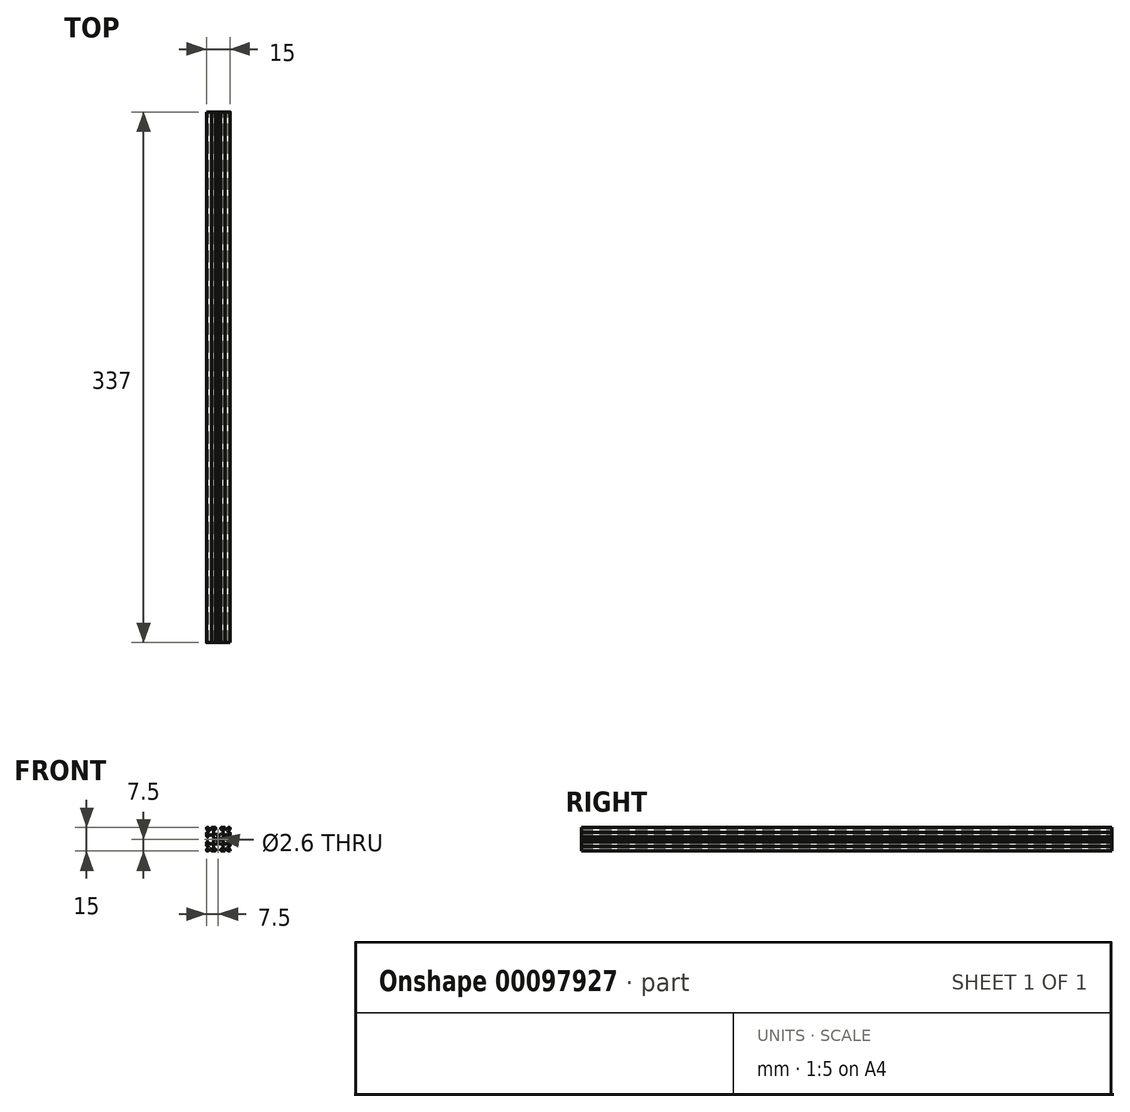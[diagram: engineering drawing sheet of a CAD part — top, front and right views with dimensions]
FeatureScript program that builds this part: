
annotation { "Feature Type Name" : "Feature", "Feature Type Description" : "" }
export const myFeature = defineFeature(function(context is Context, id is Id, definition is map)
    precondition{}
    {
        {
            var Q0;
            Q0=qCreatedBy(makeId("Front.planeOp"),FACE);
            var sketch = newSketch(context, id + "F0", { "sketchPlane" : qUnion([Q0])});
            skLineSegment(sketch, "E0.0.0", {"start": v(0.83, -2.55) * mm, "end": v(0.83, -2.77) * mm});
            skArc(sketch, "E0.0.1", {"start": v(0.83, -2.77) * mm, "mid": v(0.87, -2.9) * mm, "end": v(0.98, -2.97) * mm});
            skLineSegment(sketch, "E0.0.2", {"start": v(0.98, -2.97) * mm, "end": v(2.5, -3.31) * mm});
            skArc(sketch, "E0.0.3", {"start": v(2.5, -3.31) * mm, "mid": v(2.8, -3.49) * mm, "end": v(2.9, -3.8) * mm});
            skLineSegment(sketch, "E0.0.4", {"start": v(2.9, -3.8) * mm, "end": v(2.9, -5.9) * mm});
            skArc(sketch, "E0.0.5", {"start": v(2.9, -5.9) * mm, "mid": v(2.84, -6.04) * mm, "end": v(2.7, -6.1) * mm});
            skLineSegment(sketch, "E0.0.6", {"start": v(2.7, -6.1) * mm, "end": v(2.1, -6.1) * mm});
            skArc(sketch, "E0.0.7", {"start": v(2.1, -6.1) * mm, "mid": v(1.75, -6.25) * mm, "end": v(1.6, -6.6) * mm});
            skLineSegment(sketch, "E0.0.8", {"start": v(1.6, -6.6) * mm, "end": v(1.6, -7) * mm});
            skArc(sketch, "E0.0.9", {"start": v(1.6, -7) * mm, "mid": v(1.75, -7.35) * mm, "end": v(2.1, -7.5) * mm});
            skLineSegment(sketch, "E0.0.10", {"start": v(2.1, -7.5) * mm, "end": v(3.9, -7.5) * mm});
            skArc(sketch, "E0.0.11", {"start": v(3.9, -7.5) * mm, "mid": v(4.25, -7.35) * mm, "end": v(4.4, -7) * mm});
            skLineSegment(sketch, "E0.0.12", {"start": v(4.4, -7) * mm, "end": v(4.4, -6.67) * mm});
            skArc(sketch, "E0.0.13", {"start": v(4.4, -6.67) * mm, "mid": v(4.7, -6.2) * mm, "end": v(5.25, -6.31) * mm});
            skLineSegment(sketch, "E0.0.14", {"start": v(5.25, -6.31) * mm, "end": v(6.3, -7.35) * mm});
            skArc(sketch, "E0.0.15", {"start": v(6.3, -7.35) * mm, "mid": v(6.46, -7.46) * mm, "end": v(6.65, -7.5) * mm});
            skLineSegment(sketch, "E0.0.16", {"start": v(6.65, -7.5) * mm, "end": v(7.25, -7.5) * mm});
            skArc(sketch, "E0.0.17", {"start": v(7.25, -7.5) * mm, "mid": v(7.43, -7.43) * mm, "end": v(7.5, -7.25) * mm});
            skLineSegment(sketch, "E0.0.18", {"start": v(7.5, -7.25) * mm, "end": v(7.5, -6.65) * mm});
            skArc(sketch, "E0.0.19", {"start": v(7.5, -6.65) * mm, "mid": v(7.46, -6.46) * mm, "end": v(7.35, -6.3) * mm});
            skLineSegment(sketch, "E0.0.20", {"start": v(7.35, -6.3) * mm, "end": v(6.31, -5.25) * mm});
            skArc(sketch, "E0.0.21", {"start": v(6.31, -5.25) * mm, "mid": v(6.2, -4.7) * mm, "end": v(6.67, -4.4) * mm});
            skLineSegment(sketch, "E0.0.22", {"start": v(6.67, -4.4) * mm, "end": v(7, -4.4) * mm});
            skArc(sketch, "E0.0.23", {"start": v(7, -4.4) * mm, "mid": v(7.35, -4.25) * mm, "end": v(7.5, -3.9) * mm});
            skLineSegment(sketch, "E0.0.24", {"start": v(7.5, -3.9) * mm, "end": v(7.5, -2.1) * mm});
            skArc(sketch, "E0.0.25", {"start": v(7.5, -2.1) * mm, "mid": v(7.35, -1.75) * mm, "end": v(7, -1.6) * mm});
            skLineSegment(sketch, "E0.0.26", {"start": v(7, -1.6) * mm, "end": v(6.6, -1.6) * mm});
            skArc(sketch, "E0.0.27", {"start": v(6.6, -1.6) * mm, "mid": v(6.25, -1.75) * mm, "end": v(6.1, -2.1) * mm});
            skLineSegment(sketch, "E0.0.28", {"start": v(6.1, -2.1) * mm, "end": v(6.1, -2.7) * mm});
            skArc(sketch, "E0.0.29", {"start": v(6.1, -2.7) * mm, "mid": v(6.04, -2.84) * mm, "end": v(5.9, -2.9) * mm});
            skLineSegment(sketch, "E0.0.30", {"start": v(5.9, -2.9) * mm, "end": v(3.8, -2.9) * mm});
            skArc(sketch, "E0.0.31", {"start": v(3.8, -2.9) * mm, "mid": v(3.49, -2.8) * mm, "end": v(3.31, -2.5) * mm});
            skLineSegment(sketch, "E0.0.32", {"start": v(3.31, -2.5) * mm, "end": v(2.97, -0.98) * mm});
            skArc(sketch, "E0.0.33", {"start": v(2.97, -0.98) * mm, "mid": v(2.9, -0.87) * mm, "end": v(2.77, -0.83) * mm});
            skLineSegment(sketch, "E0.0.34", {"start": v(2.77, -0.83) * mm, "end": v(2.55, -0.83) * mm});
            skArc(sketch, "E0.0.35", {"start": v(2.55, -0.83) * mm, "mid": v(2.4, -0.77) * mm, "end": v(2.35, -0.63) * mm});
            skLineSegment(sketch, "E0.0.36", {"start": v(2.35, -0.63) * mm, "end": v(2.35, 0.63) * mm});
            skArc(sketch, "E0.0.37", {"start": v(2.35, 0.63) * mm, "mid": v(2.4, 0.77) * mm, "end": v(2.55, 0.83) * mm});
            skLineSegment(sketch, "E0.0.38", {"start": v(2.55, 0.83) * mm, "end": v(2.77, 0.83) * mm});
            skArc(sketch, "E0.0.39", {"start": v(2.77, 0.83) * mm, "mid": v(2.9, 0.87) * mm, "end": v(2.97, 0.98) * mm});
            skLineSegment(sketch, "E0.0.40", {"start": v(2.97, 0.98) * mm, "end": v(3.31, 2.5) * mm});
            skArc(sketch, "E0.0.41", {"start": v(3.31, 2.5) * mm, "mid": v(3.49, 2.8) * mm, "end": v(3.8, 2.9) * mm});
            skLineSegment(sketch, "E0.0.42", {"start": v(3.8, 2.9) * mm, "end": v(5.9, 2.9) * mm});
            skArc(sketch, "E0.0.43", {"start": v(5.9, 2.9) * mm, "mid": v(6.04, 2.84) * mm, "end": v(6.1, 2.7) * mm});
            skLineSegment(sketch, "E0.0.44", {"start": v(6.1, 2.7) * mm, "end": v(6.1, 2.1) * mm});
            skArc(sketch, "E0.0.45", {"start": v(6.1, 2.1) * mm, "mid": v(6.25, 1.75) * mm, "end": v(6.6, 1.6) * mm});
            skLineSegment(sketch, "E0.0.46", {"start": v(6.6, 1.6) * mm, "end": v(7, 1.6) * mm});
            skArc(sketch, "E0.0.47", {"start": v(7, 1.6) * mm, "mid": v(7.35, 1.75) * mm, "end": v(7.5, 2.1) * mm});
            skLineSegment(sketch, "E0.0.48", {"start": v(7.5, 2.1) * mm, "end": v(7.5, 3.9) * mm});
            skArc(sketch, "E0.0.49", {"start": v(7.5, 3.9) * mm, "mid": v(7.35, 4.25) * mm, "end": v(7, 4.4) * mm});
            skLineSegment(sketch, "E0.0.50", {"start": v(7, 4.4) * mm, "end": v(6.67, 4.4) * mm});
            skArc(sketch, "E0.0.51", {"start": v(6.67, 4.4) * mm, "mid": v(6.2, 4.7) * mm, "end": v(6.31, 5.25) * mm});
            skLineSegment(sketch, "E0.0.52", {"start": v(6.31, 5.25) * mm, "end": v(7.35, 6.3) * mm});
            skArc(sketch, "E0.0.53", {"start": v(7.35, 6.3) * mm, "mid": v(7.46, 6.46) * mm, "end": v(7.5, 6.65) * mm});
            skLineSegment(sketch, "E0.0.54", {"start": v(7.5, 6.65) * mm, "end": v(7.5, 7.25) * mm});
            skArc(sketch, "E0.0.55", {"start": v(7.5, 7.25) * mm, "mid": v(7.43, 7.43) * mm, "end": v(7.25, 7.5) * mm});
            skLineSegment(sketch, "E0.0.56", {"start": v(7.25, 7.5) * mm, "end": v(6.65, 7.5) * mm});
            skArc(sketch, "E0.0.57", {"start": v(6.65, 7.5) * mm, "mid": v(6.46, 7.46) * mm, "end": v(6.3, 7.35) * mm});
            skLineSegment(sketch, "E0.0.58", {"start": v(6.3, 7.35) * mm, "end": v(5.25, 6.31) * mm});
            skArc(sketch, "E0.0.59", {"start": v(5.25, 6.31) * mm, "mid": v(4.7, 6.2) * mm, "end": v(4.4, 6.67) * mm});
            skLineSegment(sketch, "E0.0.60", {"start": v(4.4, 6.67) * mm, "end": v(4.4, 7) * mm});
            skArc(sketch, "E0.0.61", {"start": v(4.4, 7) * mm, "mid": v(4.25, 7.35) * mm, "end": v(3.9, 7.5) * mm});
            skLineSegment(sketch, "E0.0.62", {"start": v(3.9, 7.5) * mm, "end": v(2.1, 7.5) * mm});
            skArc(sketch, "E0.0.63", {"start": v(2.1, 7.5) * mm, "mid": v(1.75, 7.35) * mm, "end": v(1.6, 7) * mm});
            skLineSegment(sketch, "E0.0.64", {"start": v(1.6, 7) * mm, "end": v(1.6, 6.6) * mm});
            skArc(sketch, "E0.0.65", {"start": v(1.6, 6.6) * mm, "mid": v(1.75, 6.25) * mm, "end": v(2.1, 6.1) * mm});
            skLineSegment(sketch, "E0.0.66", {"start": v(2.1, 6.1) * mm, "end": v(2.7, 6.1) * mm});
            skArc(sketch, "E0.0.67", {"start": v(2.7, 6.1) * mm, "mid": v(2.84, 6.04) * mm, "end": v(2.9, 5.9) * mm});
            skLineSegment(sketch, "E0.0.68", {"start": v(2.9, 5.9) * mm, "end": v(2.9, 3.8) * mm});
            skArc(sketch, "E0.0.69", {"start": v(2.9, 3.8) * mm, "mid": v(2.8, 3.49) * mm, "end": v(2.5, 3.31) * mm});
            skLineSegment(sketch, "E0.0.70", {"start": v(2.5, 3.31) * mm, "end": v(0.98, 2.97) * mm});
            skArc(sketch, "E0.0.71", {"start": v(0.98, 2.97) * mm, "mid": v(0.87, 2.9) * mm, "end": v(0.83, 2.77) * mm});
            skLineSegment(sketch, "E0.0.72", {"start": v(0.83, 2.77) * mm, "end": v(0.83, 2.55) * mm});
            skArc(sketch, "E0.0.73", {"start": v(0.83, 2.55) * mm, "mid": v(0.77, 2.4) * mm, "end": v(0.63, 2.35) * mm});
            skLineSegment(sketch, "E0.0.74", {"start": v(0.63, 2.35) * mm, "end": v(-0.63, 2.35) * mm});
            skArc(sketch, "E0.0.75", {"start": v(-0.63, 2.35) * mm, "mid": v(-0.77, 2.4) * mm, "end": v(-0.83, 2.55) * mm});
            skLineSegment(sketch, "E0.0.76", {"start": v(-0.83, 2.55) * mm, "end": v(-0.83, 2.77) * mm});
            skArc(sketch, "E0.0.77", {"start": v(-0.83, 2.77) * mm, "mid": v(-0.87, 2.9) * mm, "end": v(-0.98, 2.97) * mm});
            skLineSegment(sketch, "E0.0.78", {"start": v(-0.98, 2.97) * mm, "end": v(-2.5, 3.31) * mm});
            skArc(sketch, "E0.0.79", {"start": v(-2.5, 3.31) * mm, "mid": v(-2.8, 3.49) * mm, "end": v(-2.9, 3.8) * mm});
            skLineSegment(sketch, "E0.0.80", {"start": v(-2.9, 3.8) * mm, "end": v(-2.9, 5.9) * mm});
            skArc(sketch, "E0.0.81", {"start": v(-2.9, 5.9) * mm, "mid": v(-2.84, 6.04) * mm, "end": v(-2.7, 6.1) * mm});
            skLineSegment(sketch, "E0.0.82", {"start": v(-2.7, 6.1) * mm, "end": v(-2.1, 6.1) * mm});
            skArc(sketch, "E0.0.83", {"start": v(-2.1, 6.1) * mm, "mid": v(-1.75, 6.25) * mm, "end": v(-1.6, 6.6) * mm});
            skLineSegment(sketch, "E0.0.84", {"start": v(-1.6, 6.6) * mm, "end": v(-1.6, 7) * mm});
            skArc(sketch, "E0.0.85", {"start": v(-1.6, 7) * mm, "mid": v(-1.75, 7.35) * mm, "end": v(-2.1, 7.5) * mm});
            skLineSegment(sketch, "E0.0.86", {"start": v(-2.1, 7.5) * mm, "end": v(-3.9, 7.5) * mm});
            skArc(sketch, "E0.0.87", {"start": v(-3.9, 7.5) * mm, "mid": v(-4.25, 7.35) * mm, "end": v(-4.4, 7) * mm});
            skLineSegment(sketch, "E0.0.88", {"start": v(-4.4, 7) * mm, "end": v(-4.4, 6.67) * mm});
            skArc(sketch, "E0.0.89", {"start": v(-4.4, 6.67) * mm, "mid": v(-4.7, 6.2) * mm, "end": v(-5.25, 6.31) * mm});
            skLineSegment(sketch, "E0.0.90", {"start": v(-5.25, 6.31) * mm, "end": v(-6.3, 7.35) * mm});
            skArc(sketch, "E0.0.91", {"start": v(-6.3, 7.35) * mm, "mid": v(-6.46, 7.46) * mm, "end": v(-6.65, 7.5) * mm});
            skLineSegment(sketch, "E0.0.92", {"start": v(-6.65, 7.5) * mm, "end": v(-7.25, 7.5) * mm});
            skArc(sketch, "E0.0.93", {"start": v(-7.25, 7.5) * mm, "mid": v(-7.43, 7.43) * mm, "end": v(-7.5, 7.25) * mm});
            skLineSegment(sketch, "E0.0.94", {"start": v(-7.5, 7.25) * mm, "end": v(-7.5, 6.65) * mm});
            skArc(sketch, "E0.0.95", {"start": v(-7.5, 6.65) * mm, "mid": v(-7.46, 6.46) * mm, "end": v(-7.35, 6.3) * mm});
            skLineSegment(sketch, "E0.0.96", {"start": v(-7.35, 6.3) * mm, "end": v(-6.31, 5.25) * mm});
            skArc(sketch, "E0.0.97", {"start": v(-6.31, 5.25) * mm, "mid": v(-6.2, 4.7) * mm, "end": v(-6.67, 4.4) * mm});
            skLineSegment(sketch, "E0.0.98", {"start": v(-6.67, 4.4) * mm, "end": v(-7, 4.4) * mm});
            skArc(sketch, "E0.0.99", {"start": v(-7, 4.4) * mm, "mid": v(-7.35, 4.25) * mm, "end": v(-7.5, 3.9) * mm});
            skLineSegment(sketch, "E0.0.100", {"start": v(-7.5, 3.9) * mm, "end": v(-7.5, 2.1) * mm});
            skArc(sketch, "E0.0.101", {"start": v(-7.5, 2.1) * mm, "mid": v(-7.35, 1.75) * mm, "end": v(-7, 1.6) * mm});
            skLineSegment(sketch, "E0.0.102", {"start": v(-7, 1.6) * mm, "end": v(-6.6, 1.6) * mm});
            skArc(sketch, "E0.0.103", {"start": v(-6.6, 1.6) * mm, "mid": v(-6.25, 1.75) * mm, "end": v(-6.1, 2.1) * mm});
            skLineSegment(sketch, "E0.0.104", {"start": v(-6.1, 2.1) * mm, "end": v(-6.1, 2.7) * mm});
            skArc(sketch, "E0.0.105", {"start": v(-6.1, 2.7) * mm, "mid": v(-6.04, 2.84) * mm, "end": v(-5.9, 2.9) * mm});
            skLineSegment(sketch, "E0.0.106", {"start": v(-5.9, 2.9) * mm, "end": v(-3.8, 2.9) * mm});
            skArc(sketch, "E0.0.107", {"start": v(-3.8, 2.9) * mm, "mid": v(-3.49, 2.8) * mm, "end": v(-3.31, 2.5) * mm});
            skLineSegment(sketch, "E0.0.108", {"start": v(-3.31, 2.5) * mm, "end": v(-2.97, 0.98) * mm});
            skArc(sketch, "E0.0.109", {"start": v(-2.97, 0.98) * mm, "mid": v(-2.9, 0.87) * mm, "end": v(-2.77, 0.83) * mm});
            skLineSegment(sketch, "E0.0.110", {"start": v(-2.77, 0.83) * mm, "end": v(-2.55, 0.83) * mm});
            skArc(sketch, "E0.0.111", {"start": v(-2.55, 0.83) * mm, "mid": v(-2.4, 0.77) * mm, "end": v(-2.35, 0.63) * mm});
            skLineSegment(sketch, "E0.0.112", {"start": v(-2.35, 0.63) * mm, "end": v(-2.35, -0.63) * mm});
            skArc(sketch, "E0.0.113", {"start": v(-2.35, -0.63) * mm, "mid": v(-2.4, -0.77) * mm, "end": v(-2.55, -0.83) * mm});
            skLineSegment(sketch, "E0.0.114", {"start": v(-2.55, -0.83) * mm, "end": v(-2.77, -0.83) * mm});
            skArc(sketch, "E0.0.115", {"start": v(-2.77, -0.83) * mm, "mid": v(-2.9, -0.87) * mm, "end": v(-2.97, -0.98) * mm});
            skLineSegment(sketch, "E0.0.116", {"start": v(-2.97, -0.98) * mm, "end": v(-3.31, -2.5) * mm});
            skArc(sketch, "E0.0.117", {"start": v(-3.31, -2.5) * mm, "mid": v(-3.49, -2.8) * mm, "end": v(-3.8, -2.9) * mm});
            skLineSegment(sketch, "E0.0.118", {"start": v(-3.8, -2.9) * mm, "end": v(-5.9, -2.9) * mm});
            skArc(sketch, "E0.0.119", {"start": v(-5.9, -2.9) * mm, "mid": v(-6.04, -2.84) * mm, "end": v(-6.1, -2.7) * mm});
            skLineSegment(sketch, "E0.0.120", {"start": v(-6.1, -2.7) * mm, "end": v(-6.1, -2.1) * mm});
            skArc(sketch, "E0.0.121", {"start": v(-6.1, -2.1) * mm, "mid": v(-6.25, -1.75) * mm, "end": v(-6.6, -1.6) * mm});
            skLineSegment(sketch, "E0.0.122", {"start": v(-6.6, -1.6) * mm, "end": v(-7, -1.6) * mm});
            skArc(sketch, "E0.0.123", {"start": v(-7, -1.6) * mm, "mid": v(-7.35, -1.75) * mm, "end": v(-7.5, -2.1) * mm});
            skLineSegment(sketch, "E0.0.124", {"start": v(-7.5, -2.1) * mm, "end": v(-7.5, -3.9) * mm});
            skArc(sketch, "E0.0.125", {"start": v(-7.5, -3.9) * mm, "mid": v(-7.35, -4.25) * mm, "end": v(-7, -4.4) * mm});
            skLineSegment(sketch, "E0.0.126", {"start": v(-7, -4.4) * mm, "end": v(-6.67, -4.4) * mm});
            skArc(sketch, "E0.0.127", {"start": v(-6.67, -4.4) * mm, "mid": v(-6.2, -4.7) * mm, "end": v(-6.31, -5.25) * mm});
            skLineSegment(sketch, "E0.0.128", {"start": v(-6.31, -5.25) * mm, "end": v(-7.35, -6.3) * mm});
            skArc(sketch, "E0.0.129", {"start": v(-7.35, -6.3) * mm, "mid": v(-7.46, -6.46) * mm, "end": v(-7.5, -6.65) * mm});
            skLineSegment(sketch, "E0.0.130", {"start": v(-7.5, -6.65) * mm, "end": v(-7.5, -7.25) * mm});
            skArc(sketch, "E0.0.131", {"start": v(-7.5, -7.25) * mm, "mid": v(-7.43, -7.43) * mm, "end": v(-7.25, -7.5) * mm});
            skLineSegment(sketch, "E0.0.132", {"start": v(-7.25, -7.5) * mm, "end": v(-6.65, -7.5) * mm});
            skArc(sketch, "E0.0.133", {"start": v(-6.65, -7.5) * mm, "mid": v(-6.46, -7.46) * mm, "end": v(-6.3, -7.35) * mm});
            skLineSegment(sketch, "E0.0.134", {"start": v(-6.3, -7.35) * mm, "end": v(-5.25, -6.31) * mm});
            skArc(sketch, "E0.0.135", {"start": v(-5.25, -6.31) * mm, "mid": v(-4.7, -6.2) * mm, "end": v(-4.4, -6.67) * mm});
            skLineSegment(sketch, "E0.0.136", {"start": v(-4.4, -6.67) * mm, "end": v(-4.4, -7) * mm});
            skArc(sketch, "E0.0.137", {"start": v(-4.4, -7) * mm, "mid": v(-4.25, -7.35) * mm, "end": v(-3.9, -7.5) * mm});
            skLineSegment(sketch, "E0.0.138", {"start": v(-3.9, -7.5) * mm, "end": v(-2.1, -7.5) * mm});
            skArc(sketch, "E0.0.139", {"start": v(-2.1, -7.5) * mm, "mid": v(-1.75, -7.35) * mm, "end": v(-1.6, -7) * mm});
            skLineSegment(sketch, "E0.0.140", {"start": v(-1.6, -7) * mm, "end": v(-1.6, -6.6) * mm});
            skArc(sketch, "E0.0.141", {"start": v(-1.6, -6.6) * mm, "mid": v(-1.75, -6.25) * mm, "end": v(-2.1, -6.1) * mm});
            skLineSegment(sketch, "E0.0.142", {"start": v(-2.1, -6.1) * mm, "end": v(-2.7, -6.1) * mm});
            skArc(sketch, "E0.0.143", {"start": v(-2.7, -6.1) * mm, "mid": v(-2.84, -6.04) * mm, "end": v(-2.9, -5.9) * mm});
            skLineSegment(sketch, "E0.0.144", {"start": v(-2.9, -5.9) * mm, "end": v(-2.9, -3.8) * mm});
            skArc(sketch, "E0.0.145", {"start": v(-2.9, -3.8) * mm, "mid": v(-2.8, -3.49) * mm, "end": v(-2.5, -3.31) * mm});
            skLineSegment(sketch, "E0.0.146", {"start": v(-2.5, -3.31) * mm, "end": v(-0.98, -2.97) * mm});
            skArc(sketch, "E0.0.147", {"start": v(-0.98, -2.97) * mm, "mid": v(-0.87, -2.9) * mm, "end": v(-0.83, -2.77) * mm});
            skLineSegment(sketch, "E0.0.148", {"start": v(-0.83, -2.77) * mm, "end": v(-0.83, -2.55) * mm});
            skArc(sketch, "E0.0.149", {"start": v(-0.83, -2.55) * mm, "mid": v(-0.77, -2.4) * mm, "end": v(-0.63, -2.35) * mm});
            skLineSegment(sketch, "E0.0.150", {"start": v(-0.63, -2.35) * mm, "end": v(0.63, -2.35) * mm});
            skArc(sketch, "E0.0.151", {"start": v(0.63, -2.35) * mm, "mid": v(0.77, -2.4) * mm, "end": v(0.83, -2.55) * mm});
            skPoint(sketch, "E1", {"position": v(0, 0) * mm});
            skPoint(sketch, "E1.positionSnap0", {"position": v(0, 2.35) * mm});
            skPoint(sketch, "E1.positionSnap1", {"position": v(2.35, 0) * mm});
            skCircle(sketch, "E2", {"center": v(0, 0) * mm, "radius": 1.3 * mm});
            skSolve(sketch);
        }
        {
            var Q0;
            Q0=makeQuery(id+"F0.imprint","IMPRINT",FACE,{"disambiguationData":[TD([[makeQuery(id+"F0.imprint","IMPRINT",EDGE,{"derivedFrom":sQuery(id+"F0.wireOp",EDGE,"E0.0.0")}),1.0]])]});
            extrude(context, id + "F1", {"entities" : qUnion([Q0]), "endBound" : BoundingType.SYMMETRIC, "depth" : 337 * mm});
        }
    });
